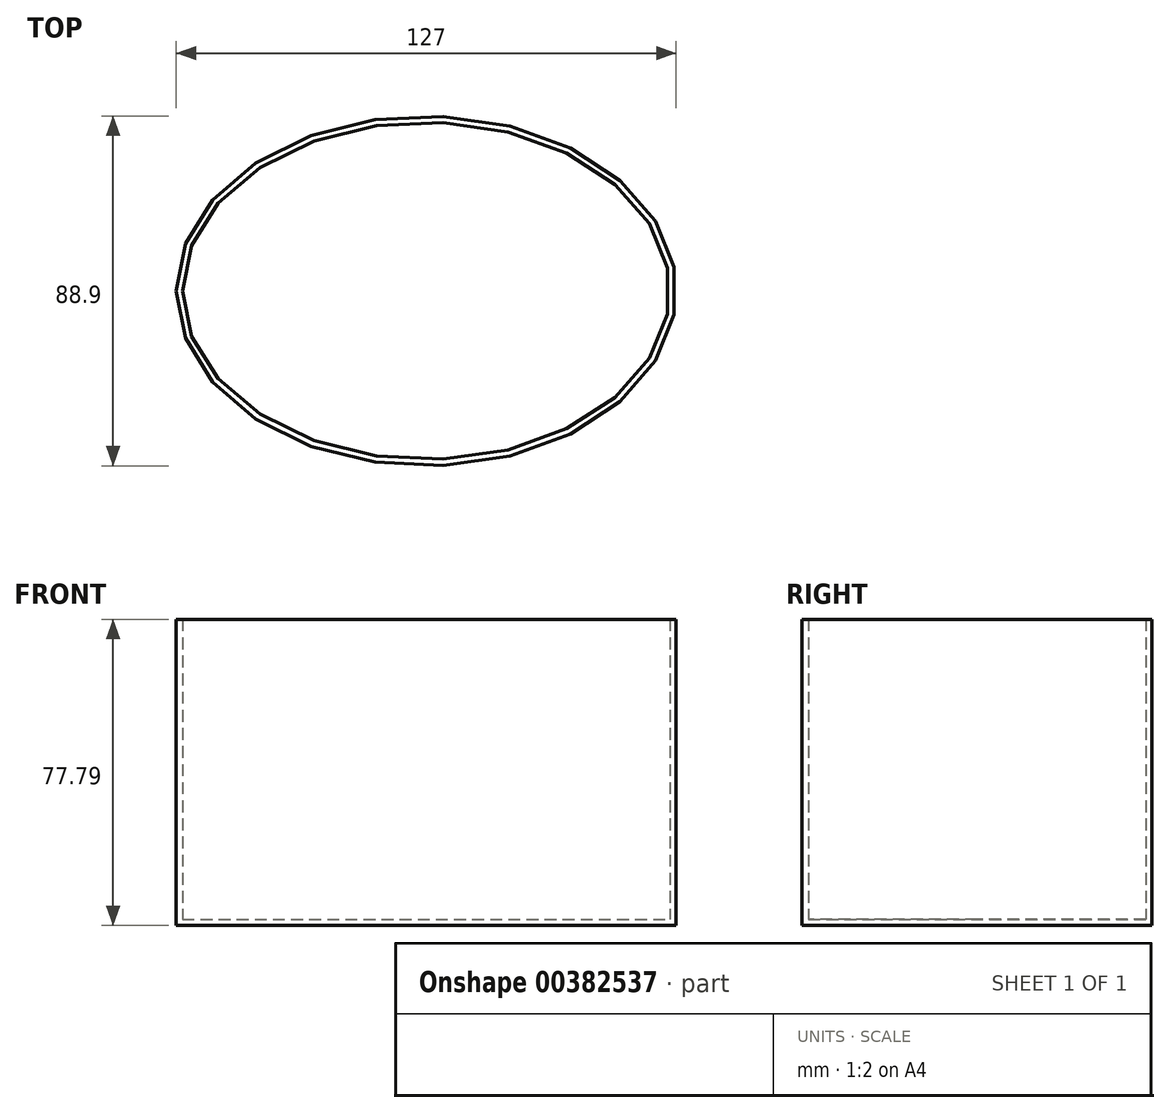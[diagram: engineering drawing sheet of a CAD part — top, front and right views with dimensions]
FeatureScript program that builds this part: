
annotation { "Feature Type Name" : "Feature", "Feature Type Description" : "" }
export const myFeature = defineFeature(function(context is Context, id is Id, definition is map)
    precondition{}
    {
        {
            var Q0;
            Q0=qCreatedBy(makeId("Top.planeOp"),FACE);
            var sketch = newSketch(context, id + "F0", { "sketchPlane" : qUnion([Q0])});
            skEllipse(sketch, "E0", {"center": v(0, 0) * mm, "majorRadius": 63.5 * mm, "minorRadius": 44.45 * mm, "majorAxis": v(-1, 0)});
            skSolve(sketch);
        }
        {
            var Q0;
            Q0=makeQuery(id+"F0.imprint","IMPRINT",FACE,{"disambiguationData":[TD([[makeQuery(id+"F0.imprint","IMPRINT",EDGE,{"derivedFrom":sQuery(id+"F0.wireOp",EDGE,"E0")}),1.0]])]});
            extrude(context, id + "F1", {"entities" : qUnion([Q0]), "depth" : 1.59 * mm});
        }
        {
            var Q0;
            Q0=makeQuery(id+"F1.opExtrude","CAP_FACE",FACE,{"disambiguationData":[OSD([sQuery(id+"F0.wireOp",EDGE,"E0")])],"isStart":false});
            var sketch = newSketch(context, id + "F2", { "sketchPlane" : qUnion([Q0])});
            skEllipse(sketch, "E1", {"center": v(0, 0) * mm, "majorRadius": 61.91 * mm, "minorRadius": 42.86 * mm, "majorAxis": v(-1, 0)});
            skSolve(sketch);
        }
        {
            var Q0;
            Q0=makeQuery(id+"F2.imprint","IMPRINT",FACE,{"disambiguationData":[TD([[makeQuery(id+"F2.imprint","IMPRINT",EDGE,{"derivedFrom":sQuery(id+"F2.wireOp",EDGE,"E1")}),-1.0]])]});
            extrude(context, id + "F3", {"entities" : qUnion([Q0]), "operationType" : NewBodyOperationType.ADD, "depth" : 76.2 * mm});
        }
    });
